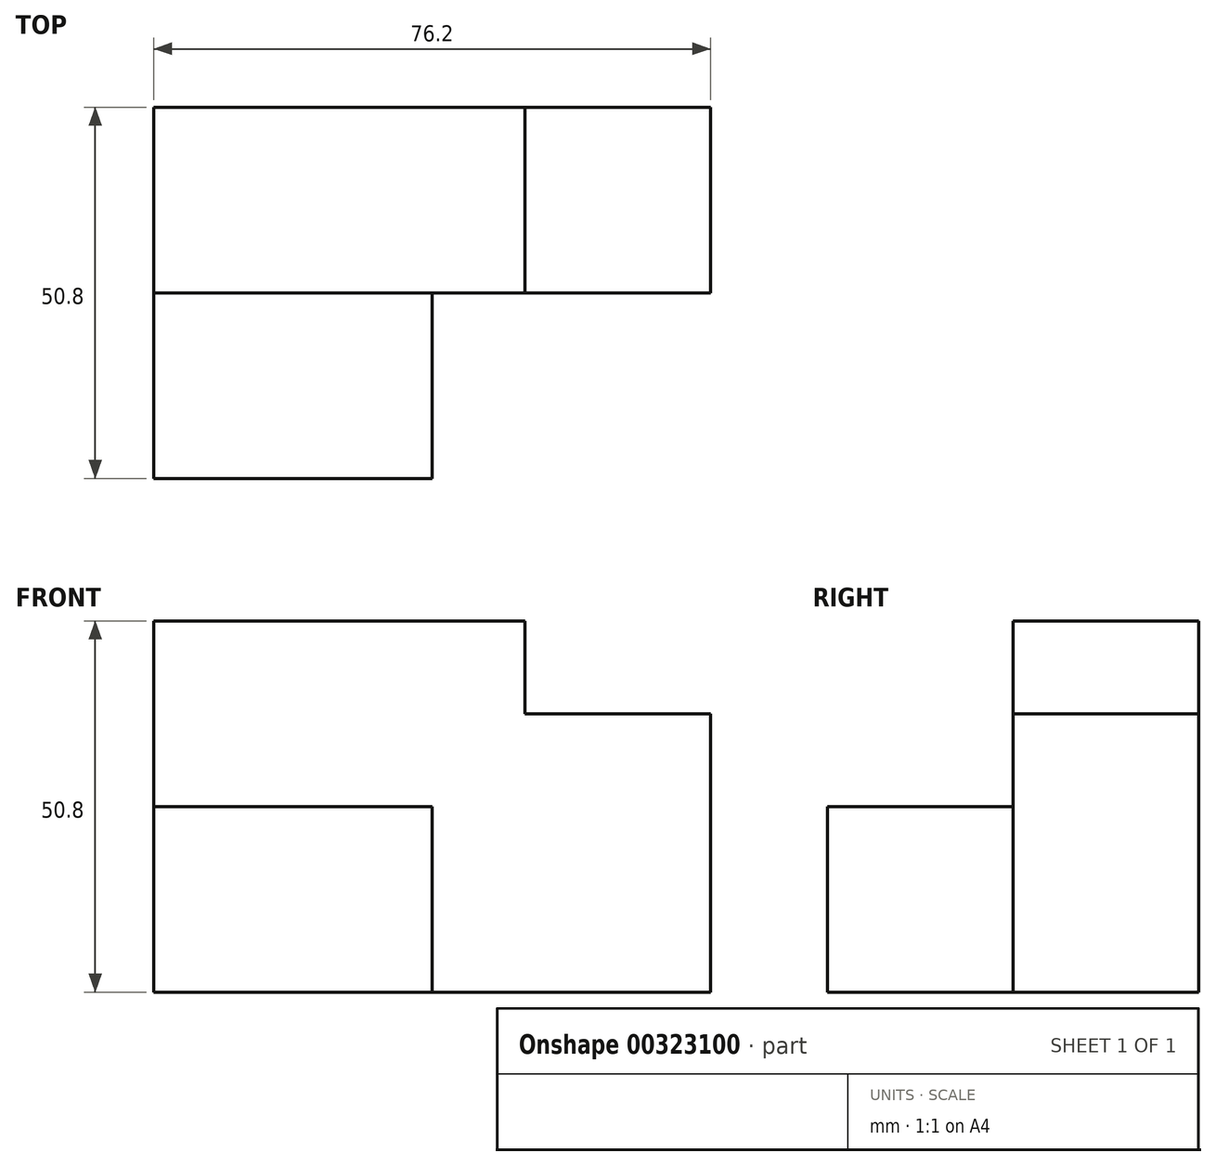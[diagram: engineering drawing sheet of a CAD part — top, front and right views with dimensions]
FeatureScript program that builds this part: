
annotation { "Feature Type Name" : "Feature", "Feature Type Description" : "" }
export const myFeature = defineFeature(function(context is Context, id is Id, definition is map)
    precondition{}
    {
        {
            var Q0;
            Q0=qCreatedBy(makeId("Front.planeOp"),FACE);
            var sketch = newSketch(context, id + "F0", { "sketchPlane" : qUnion([Q0])});
            skLineSegment(sketch, "E0", {"start": v(-69.75, 28.77) * mm, "end": v(-18.95, 28.77) * mm});
            skLineSegment(sketch, "E1", {"start": v(-18.95, 28.77) * mm, "end": v(-18.95, 16.07) * mm});
            skLineSegment(sketch, "E2", {"start": v(-18.95, 16.07) * mm, "end": v(6.45, 16.07) * mm});
            skLineSegment(sketch, "E3", {"start": v(6.45, 16.07) * mm, "end": v(6.45, -22.03) * mm});
            skLineSegment(sketch, "E4", {"start": v(6.45, -22.03) * mm, "end": v(-69.75, -22.03) * mm});
            skLineSegment(sketch, "E5", {"start": v(-69.75, -22.03) * mm, "end": v(-69.75, 28.77) * mm});
            skSolve(sketch);
        }
        {
            var Q0;
            Q0=makeQuery(id+"F0.imprint","IMPRINT",FACE,{"disambiguationData":[TD([[makeQuery(id+"F0.imprint","IMPRINT",EDGE,{"derivedFrom":sQuery(id+"F0.wireOp",EDGE,"E0")}),-1.0]])]});
            extrude(context, id + "F1", {"entities" : qUnion([Q0]), "depth" : 25.4 * mm});
        }
        {
            var Q0;
            Q0=makeQuery(id+"F1.opExtrude","CAP_FACE",FACE,{"disambiguationData":[OSD([sQuery(id+"F0.wireOp",EDGE,"E0"),sQuery(id+"F0.wireOp",EDGE,"E1"),sQuery(id+"F0.wireOp",EDGE,"E2"),sQuery(id+"F0.wireOp",EDGE,"E3"),sQuery(id+"F0.wireOp",EDGE,"E4"),sQuery(id+"F0.wireOp",EDGE,"E5")])],"isStart":false});
            var sketch = newSketch(context, id + "F2", { "sketchPlane" : qUnion([Q0])});
            skLineSegment(sketch, "E6", {"start": v(-31.65, 3.37) * mm, "end": v(-31.65, -22.03) * mm});
            skLineSegment(sketch, "E7", {"start": v(-31.65, 3.37) * mm, "end": v(-69.75, 3.37) * mm});
            skSolve(sketch);
        }
        {
            var Q0;
            Q0 = qSketchRegion(id + "F2", true);
            var Q1;
            {var subQ0=sQuery(id+"F2.wireOp",EDGE,"E6");Q1=makeQuery(id+"F2.imprint","IMPRINT",FACE,{"disambiguationData":[TD([[makeQuery(id+"F2.imprint","IMPRINT",EDGE,{"derivedFrom":subQ0}),-1.0]])]});}
            extrude(context, id + "F3", {"entities" : qUnion([Q0, Q1]), "operationType" : NewBodyOperationType.ADD, "depth" : 25.4 * mm});
        }
    });
